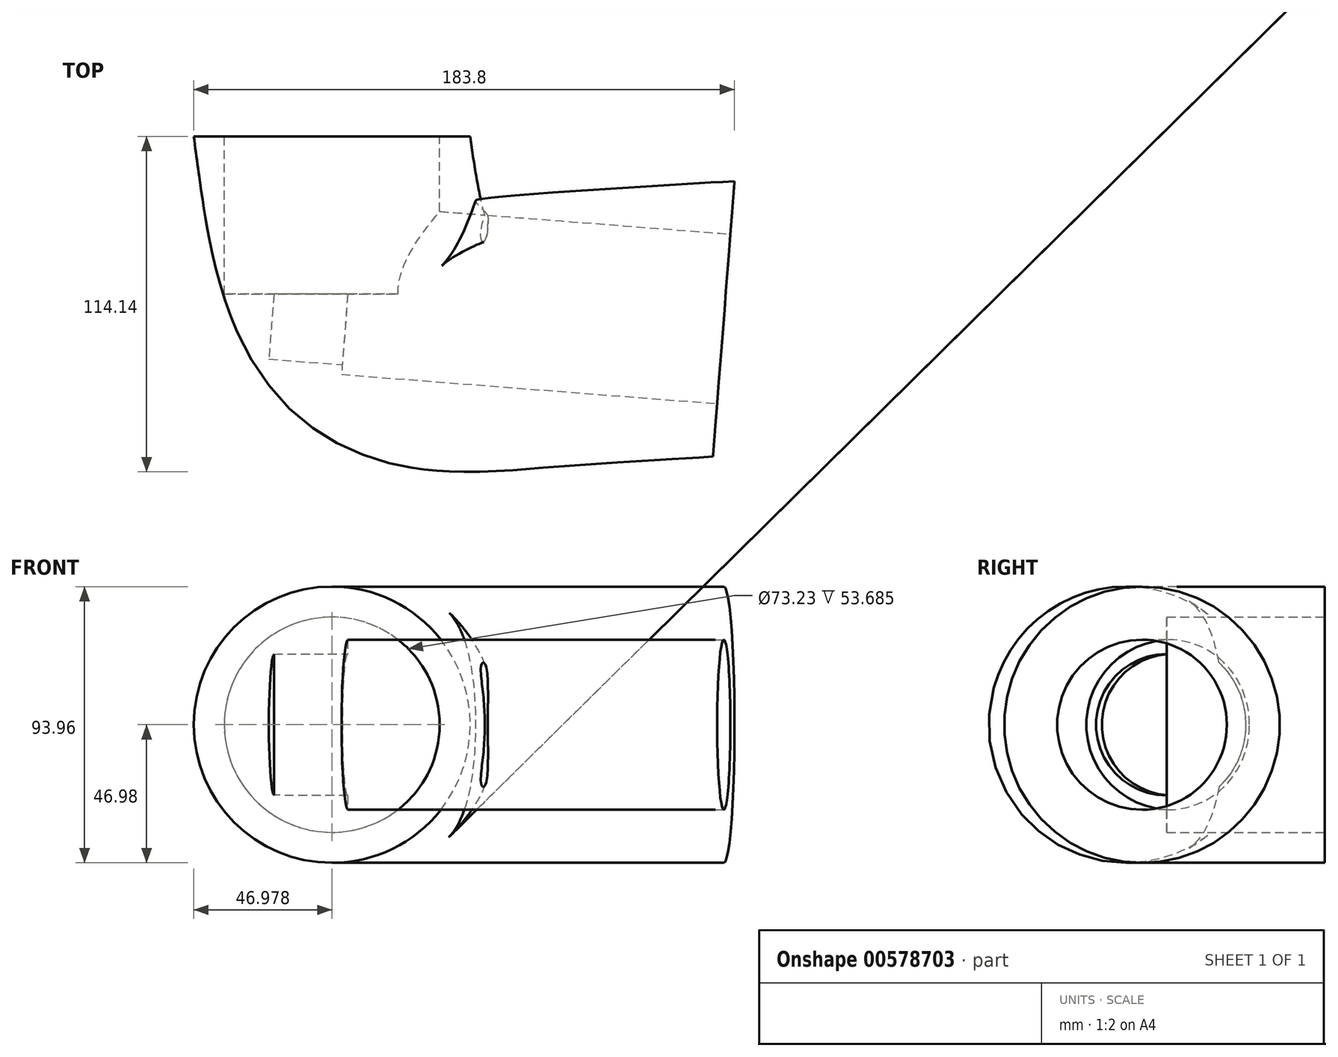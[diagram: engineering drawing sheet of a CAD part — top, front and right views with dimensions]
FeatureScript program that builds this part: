
annotation { "Feature Type Name" : "Feature", "Feature Type Description" : "" }
export const myFeature = defineFeature(function(context is Context, id is Id, definition is map)
    precondition{}
    {
        {
            var Q0;
            Q0=qCreatedBy(makeId("Front.planeOp"),FACE);
            var sketch = newSketch(context, id + "F0", { "sketchPlane" : qUnion([Q0])});
            skCircle(sketch, "E0", {"center": v(-46.98, 0) * mm, "radius": 46.98 * mm});
            skSolve(sketch);
        }
        {
            var Q0;
            Q0=qCreatedBy(makeId("Top.planeOp"),FACE);
            var sketch = newSketch(context, id + "F1", { "sketchPlane" : qUnion([Q0])});
            skFitSpline(sketch, "E1", {"points": [v(-47.22, 0) * mm, v(-27.47, -60.47) * mm, v(21.18, -66.56) * mm, v(86.18, -62.32) * mm], "startDerivative": vector(29.72, -216.2) * mm, "endDerivative": vector(186.02, 10.98) * mm});
            skSolve(sketch);
        }
        {
            var Q0;
            Q0=makeQuery(id+"F0.imprint","IMPRINT",FACE,{"disambiguationData":[TD([[makeQuery(id+"F0.imprint","IMPRINT",EDGE,{"derivedFrom":sQuery(id+"F0.wireOp",EDGE,"E0")}),1.0]])]});
            var Q1;
            Q1=sQuery(id+"F1.wireOp",EDGE,"E1");
            sweep(context, id + "F2", {"profiles" : qUnion([Q0]), "path" : qUnion([Q1])});
        }
        {
            var Q0;
            Q0=makeQuery(id+"F2.opSweep","CAP_FACE",FACE,{"disambiguationData":[OSD([sQuery(id+"F0.wireOp",EDGE,"E0"),sQuery(id+"F1.wireOp",VERTEX,"E1.start")])],"isStart":true});
            var sketch = newSketch(context, id + "F3", { "sketchPlane" : qUnion([Q0])});
            skCircle(sketch, "E2", {"center": v(46.98, 0) * mm, "radius": 36.61 * mm});
            skSolve(sketch);
        }
        {
            var Q0;
            Q0 = qSketchRegion(id + "F3", true);
            extrude(context, id + "F4", {"entities" : qUnion([Q0]), "operationType" : NewBodyOperationType.REMOVE, "oppositeDirection" : true, "depth" : 53.69 * mm, "offsetDistance" : 25.4 * mm});
        }
        {
            var Q0;
            Q0=makeQuery(id+"F2.opSweep","CAP_FACE",FACE,{"disambiguationData":[OSD([sQuery(id+"F0.wireOp",EDGE,"E0"),sQuery(id+"F1.wireOp",VERTEX,"E1.end")])],"isStart":false});
            var sketch = newSketch(context, id + "F5", { "sketchPlane" : qUnion([Q0])});
            skCircle(sketch, "E3", {"center": v(-55.2, 0) * mm, "radius": 28.92 * mm});
            skSolve(sketch);
        }
        {
            var Q0;
            Q0 = qSketchRegion(id + "F5", true);
            extrude(context, id + "F6", {"entities" : qUnion([Q0]), "operationType" : NewBodyOperationType.REMOVE, "oppositeDirection" : true, "depth" : 128.07 * mm, "offsetDistance" : 25.4 * mm});
        }
        {
            var Q0;
            Q0=makeQuery(id+"F6.boolean.opBoolean","COPY",FACE,{"derivedFrom":makeQuery(id+"F6.opExtrude","CAP_FACE",FACE,{"disambiguationData":[OSD([sQuery(id+"F5.wireOp",EDGE,"E3")])],"isStart":false})});
            var sketch = newSketch(context, id + "F7", { "sketchPlane" : qUnion([Q0])});
            skArc(sketch, "E4", {"start": v(-56.75, 24.07) * mm, "mid": v(-80.82, 0) * mm, "end": v(-56.75, -24.07) * mm});
            skSolve(sketch);
        }
        {
            var Q0;
            {var subQ0=sQuery(id+"F7.wireOp",EDGE,"E4");Q0=makeQuery(id+"F7.imprint","IMPRINT",FACE,{"disambiguationData":[TD([[makeQuery(id+"F7.imprint","IMPRINT",EDGE,{"derivedFrom":subQ0}),1.0]])]});}
            extrude(context, id + "F8", {"entities" : qUnion([Q0]), "operationType" : NewBodyOperationType.REMOVE, "oppositeDirection" : true, "depth" : 25.03 * mm, "offsetDistance" : 25.4 * mm});
        }
    });
